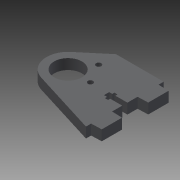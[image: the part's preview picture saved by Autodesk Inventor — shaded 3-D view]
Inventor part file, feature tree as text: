
AUTODESK INVENTOR PART (.ipt)
format: ipt  version: 2013 (Build 170138000, 138)  size: 135,680 bytes
history: native  units: mm
features: extrude x1, sketch x1
ambient origin geometry x8: Origin, YZ Plane, XZ Plane, XY Plane, X Axis, Y Axis, Z Axis, Center Point
bodies: Solid1 (feature_tree)
feature tree (2):
  extrude  "Extrusion1"  Depth=3.0mm
  sketch  "Sketch1"  dims[d0=3.0mm d2=3.0mm d3=16.1mm d4=13.0mm d5=13.0mm d6=34.0mm d7=21.6mm d9=3.0mm d10=1.25mm d11=1.25mm d12=1.8mm d13=1.8mm d14=7.0mm d15=12.2mm d16=11.8mm d17=0.2mm d18=6.0mm d19=12.2mm d20=11.8mm d21=0.2mm d22=14.8mm d23=5.9mm d24=3.0mm d25=6.0mm d26=0.0mm d27=60.0deg d28=3.0mm d29=25.0mm]
